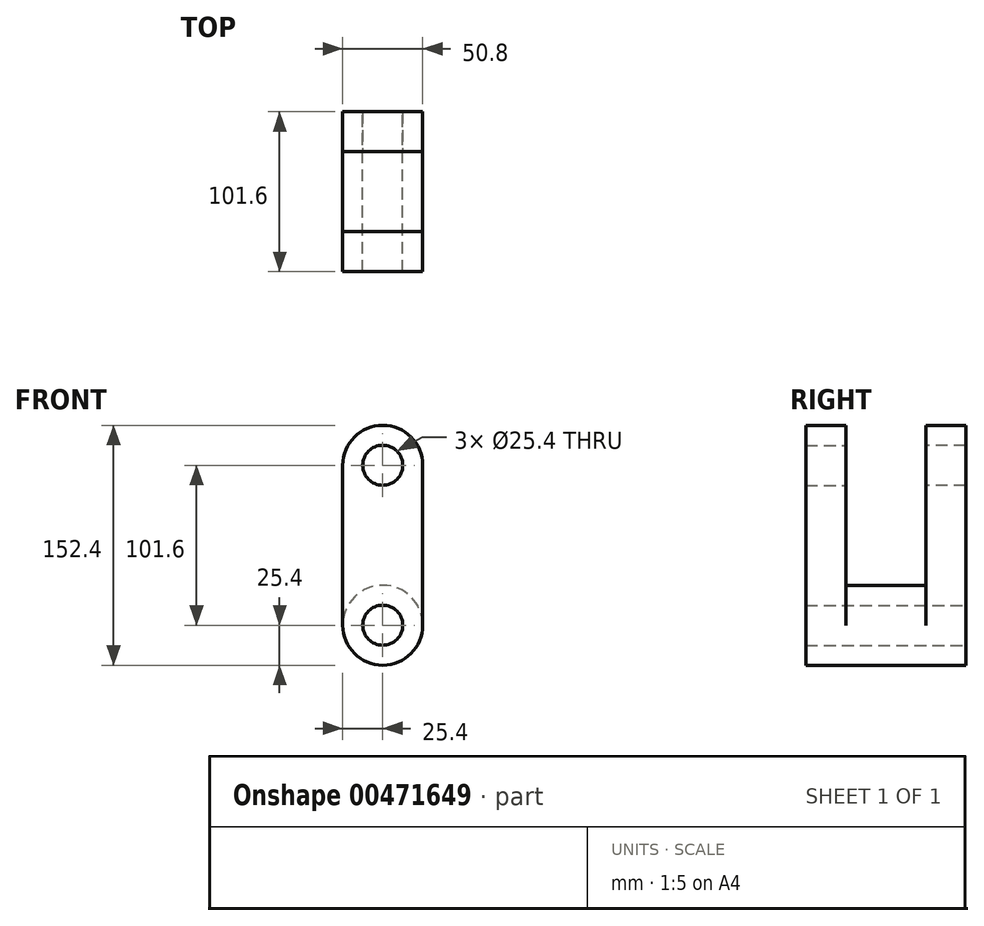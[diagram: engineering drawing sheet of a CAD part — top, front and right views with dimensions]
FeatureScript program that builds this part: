
annotation { "Feature Type Name" : "Feature", "Feature Type Description" : "" }
export const myFeature = defineFeature(function(context is Context, id is Id, definition is map)
    precondition{}
    {
        {
            var Q0;
            Q0=qCreatedBy(makeId("Front.planeOp"),FACE);
            var sketch = newSketch(context, id + "F0", { "sketchPlane" : qUnion([Q0])});
            skLineSegment(sketch, "E0", {"start": v(0, 50.8) * mm, "end": v(0, -50.8) * mm, "construction": true});
            skArc(sketch, "E1.0.startCap", {"start": v(-25.4, 50.8) * mm, "mid": v(0, 76.2) * mm, "end": v(25.4, 50.8) * mm});
            skArc(sketch, "E1.0.endCap", {"start": v(25.4, -50.8) * mm, "mid": v(0, -76.2) * mm, "end": v(-25.4, -50.8) * mm});
            skLineSegment(sketch, "E1.0.left", {"start": v(25.4, 50.8) * mm, "end": v(25.4, -50.8) * mm});
            skLineSegment(sketch, "E1.0.right", {"start": v(-25.4, 50.8) * mm, "end": v(-25.4, -50.8) * mm});
            skCircle(sketch, "E2", {"center": v(0, 50.8) * mm, "radius": 12.7 * mm});
            skCircle(sketch, "E3.MirrorC", {"center": v(0, -50.8) * mm, "radius": 12.7 * mm});
            skSolve(sketch);
        }
        {
            var Q0;
            Q0 = qSketchRegion(id + "F0", true);
            extrude(context, id + "F1", {"entities" : qUnion([Q0]), "depth" : 25.4 * mm});
        }
        {
            var Q0;
            Q0=makeQuery(id+"F1.opExtrude","CAP_FACE",FACE,{"disambiguationData":[OSD([sQuery(id+"F0.wireOp",EDGE,"E1.0.startCap"),sQuery(id+"F0.wireOp",EDGE,"E1.0.endCap"),sQuery(id+"F0.wireOp",EDGE,"E1.0.left"),sQuery(id+"F0.wireOp",EDGE,"E1.0.right"),sQuery(id+"F0.wireOp",EDGE,"E2"),sQuery(id+"F0.wireOp",EDGE,"E3.MirrorC")])],"isStart":true});
            var sketch = newSketch(context, id + "F2", { "sketchPlane" : qUnion([Q0])});
            skCircle(sketch, "E4", {"center": v(0, -50.8) * mm, "radius": 25.4 * mm});
            skSolve(sketch);
        }
        {
            var Q0;
            Q0 = qSketchRegion(id + "F2", true);
            extrude(context, id + "F3", {"entities" : qUnion([Q0]), "operationType" : NewBodyOperationType.ADD, "depth" : 25.4 * mm});
        }
        {
            var Q0;
            Q0=makeQuery(id+"F1.opExtrude","CAP_FACE",FACE,{"disambiguationData":[OSD([sQuery(id+"F0.wireOp",EDGE,"E1.0.startCap"),sQuery(id+"F0.wireOp",EDGE,"E1.0.endCap"),sQuery(id+"F0.wireOp",EDGE,"E1.0.left"),sQuery(id+"F0.wireOp",EDGE,"E1.0.right"),sQuery(id+"F0.wireOp",EDGE,"E2"),sQuery(id+"F0.wireOp",EDGE,"E3.MirrorC")])],"isStart":false});
            var sketch = newSketch(context, id + "F4", { "sketchPlane" : qUnion([Q0])});
            skCircle(sketch, "E5.0", {"center": v(0, -50.8) * mm, "radius": 12.7 * mm});
            skSolve(sketch);
        }
        {
            var Q0;
            Q0 = qSketchRegion(id + "F4", true);
            extrude(context, id + "F5", {"entities" : qUnion([Q0]), "operationType" : NewBodyOperationType.REMOVE, "endBound" : BoundingType.THROUGH_ALL, "oppositeDirection" : true, "depth" : 25.4 * mm});
        }
        {
            var Q0;
            Q0=makeQuery(id+"F1.opExtrude","SWEPT_BODY",BODY,{"disambiguationData":[OSD([sQuery(id+"F0.wireOp",EDGE,"E1.0.startCap"),sQuery(id+"F0.wireOp",EDGE,"E1.0.endCap"),sQuery(id+"F0.wireOp",EDGE,"E1.0.left"),sQuery(id+"F0.wireOp",EDGE,"E1.0.right"),sQuery(id+"F0.wireOp",EDGE,"E2"),sQuery(id+"F0.wireOp",EDGE,"E3.MirrorC")])]});
            var Q1;
            Q1=makeQuery(id+"F3.opExtrude","CAP_FACE",FACE,{"disambiguationData":[OSD([sQuery(id+"F2.wireOp",EDGE,"E4")])],"isStart":false});
            mirror(context, id + "F6", {"operationType" : NewBodyOperationType.ADD, "entities" : qUnion([Q0]), "mirrorPlane" : qUnion([Q1])});
        }
    });
